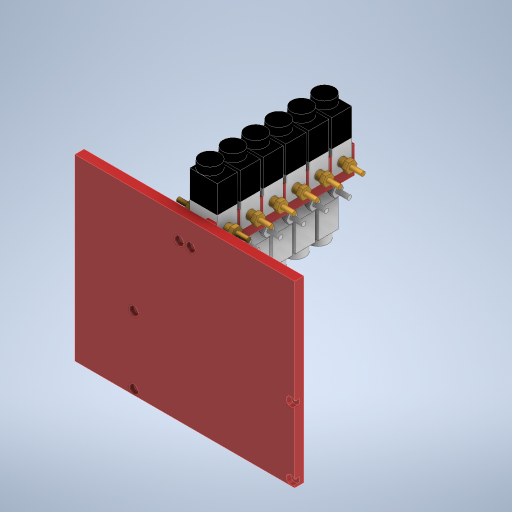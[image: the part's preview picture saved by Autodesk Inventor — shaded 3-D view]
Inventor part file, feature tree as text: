
AUTODESK INVENTOR PART (.ipt)
format: ipt  version: 2024.2 (Build 282272000, 272)  size: 1,242,112 bytes
history: native  units: mm
features: other x37, extrude x15, sketch x13, projected_geometry x11, mirror x2, pattern_linear x2, pattern_circular x2, plane x1, chamfer x1
ambient origin geometry x8: Origin, YZ Plane, XZ Plane, XY Plane, X Axis, Y Axis, Z Axis, Center Point
bodies: Solid6 (feature_tree), Solid8 (feature_tree), Solid11 (feature_tree), Solid14 (feature_tree), Solid17 (feature_tree), Solid20 (feature_tree), Solid7 (feature_tree), Solid10 (feature_tree), Solid13 (feature_tree), Solid16 (feature_tree), Solid19 (feature_tree), Solid9 (feature_tree), Solid12 (feature_tree), Solid15 (feature_tree), Solid18 (feature_tree), Solid21 (feature_tree), Solid48 (feature_tree), Solid53 (feature_tree), Solid47 (feature_tree), Solid52 (feature_tree), Solid46 (feature_tree), Solid51 (feature_tree), Solid45 (feature_tree), Solid50 (feature_tree), Solid44 (feature_tree), Solid49 (feature_tree), Solid42 (feature_tree), Solid41 (feature_tree), Solid43 (feature_tree), Solid54 (feature_tree), Solid55 (feature_tree), Solid56 (feature_tree), Solid57 (feature_tree), Solid58 (feature_tree)
feature tree (84):
  other  "Valvula P1"
  extrude  "Extrusion1"  Depth=30.0mm
  extrude  "Extrusion2"  Depth=5.0mm
  extrude  "Extrusion3"  Depth=27.0mm TaperAngle=0.0deg
  extrude  "Extrusion4"  Depth=8.5mm TaperAngle=0.0deg
  plane  "Work Plane1"
  mirror  "Mirror1"
  extrude  "Extrusion5"  Depth=10.0mm
  extrude  "Extrusion6"  Depth=11.4mm TaperAngle=0.0deg
  sketch  "Sketch7"  dims[d17=10.6mm d18=0.0mm d19=11.0mm]
  extrude  "Extrusion7"  Depth=11.0mm
  extrude  "Extrusion8"  Depth=4.6mm
  mirror  "Mirror2"
  pattern_linear  "Rectangular Pattern1"  Count1=6 Spacing1=25.0mm
  sketch  "Sketch9"  dims[d20=4.6mm d21=0.0mm d22=4.8mm]
  extrude  "Extrusion9"  Depth=10.0mm
  extrude  "Extrusion12"  Depth=6.0mm TaperAngle=0.0deg
  extrude  "Extrusion10"  Depth=20.0mm TaperAngle=360.0deg
  sketch  "Sketch12"  dims[d33=10.0mm d34=0.0mm d35=0.1mm]
  other  "Work Axis1"
  extrude  "Extrusion13"  Depth=0.05mm
  pattern_linear  "Rectangular Pattern2"  Spacing1=0.05mm  [1 undecoded]
  chamfer  "Chamfer2"  Distance=10.0mm
  pattern_circular  "Circular Pattern2"  Count=6  [1 undecoded]
  pattern_circular  "Circular Pattern3"  Count=2  [1 undecoded]
  extrude  "Extrusion14"  Depth=20.0mm TaperAngle=45.0deg
  extrude  "Extrusion17"  Depth=20.0mm TaperAngle=360.0deg
  extrude  "Extrusion18"  Depth=5.0mm
  sketch  "Sketch1"  dims[d0=22.0mm d1=30.0mm]
  sketch  "Sketch2"  dims[d2=15.0mm d3=5.0mm]
  projected_geometry  "Projected Loop1"
  other  "Valvula P2"
  sketch  "Sketch3"  dims[d4=4.0mm d5=27.0mm d6=0.0mm]
  sketch  "Sketch4"  dims[d7=30.0mm d8=0.0mm d9=8.5mm d10=0.0mm]
  sketch  "Sketch5"  dims[d11=10.0mm d12=9.4mm]
  other  "Valvula P3"
  sketch  "Sketch6"  dims[d13=11.4mm d14=0.0mm d15=11.4mm d16=0.0mm]
  projected_geometry  "Projected Loop2"
  projected_geometry  "Projected Loop3"
  projected_geometry  "Projected Loop5"
  other  "Pattern of Valvula P2:1"
  other  "Pattern of Valvula P2:2"
  other  "Pattern of Valvula P2:3"
  other  "Pattern of Valvula P2:4"
  other  "Pattern of Valvula P2:5"
  other  "Pattern of Valvula P1:6"
  other  "Pattern of Valvula P1:7"
  other  "Pattern of Valvula P1:8"
  other  "Pattern of Valvula P1:9"
  other  "Pattern of Valvula P1:10"
  other  "Pattern of Valvula P3:11"
  other  "Pattern of Valvula P3:12"
  other  "Pattern of Valvula P3:13"
  other  "Pattern of Valvula P3:14"
  other  "Pattern of Valvula P3:15"
  projected_geometry  "Projected Loop11"
  projected_geometry  "Projected Loop12"
  projected_geometry  "Projected Loop13"
  projected_geometry  "Projected Loop14"
  projected_geometry  "Projected Loop15"
  sketch  "Sketch10"  dims[d23=12.7mm d24=0.0mm d25=60.0mm d27=25.0mm]
  projected_geometry  "Projected Loop16"
  sketch  "Sketch13"  dims[d36=3.0mm d44=6.0mm d45=0.0mm]
  other  "Pattern of Solid20:35"
  other  "Pattern of Solid19:36"
  other  "Pattern of Solid17:37"
  other  "Pattern of Solid16:38"
  other  "Pattern of Solid14:39"
  other  "Pattern of Solid13:40"
  other  "Pattern of Solid11:41"
  other  "Pattern of Solid10:42"
  other  "Pattern of Solid8:43"
  other  "Pattern of Solid7:44"
  other  "Pattern of Valvula P2:45"
  other  "Pattern of Valvula P1:46"
  other  "Pattern of Valvula P3:47"
  other  "Pattern of Solid9:48"
  other  "Pattern of Solid12:49"
  other  "Pattern of Solid15:50"
  other  "Pattern of Solid18:51"
  other  "Pattern of Solid21:52"
  sketch  "Sketch14"  dims[d59=0.0mm d60=0.0mm d61=20.0mm d62=360.0deg]
  sketch  "Sketch16"  dims[d64=7.3mm d65=0.05mm d66=0.05mm d67=10.0mm d68=0.0mm d69=60.0mm d71=25.0mm d72=20.0mm d73=20.0mm d74=2.0mm d75=45.0deg d76=20.0mm d77=360.0deg d79=5.0mm d80=12.5mm d81=10.0mm d82=0.0mm d83=3.0mm d84=20.0mm d86=25.0mm d88=74.0mm d89=171.5mm d90=3.3mm d91=180.0mm d92=85.0mm d93=107.0mm d95=3.3mm d96=3.3mm d105=2.0mm d106=195.5mm d107=15.0mm d108=240.0mm d109=10.0mm d110=0.0mm d111=58.0mm d112=10.0mm d113=5.0mm d114=0.0mm]
  projected_geometry  "Projected Loop18"
note: 3 required parameter values undecoded (feature->parameter linkage not recoverable at this tier; creation-order binding heuristic only, values carry confidence <= 0.55)
